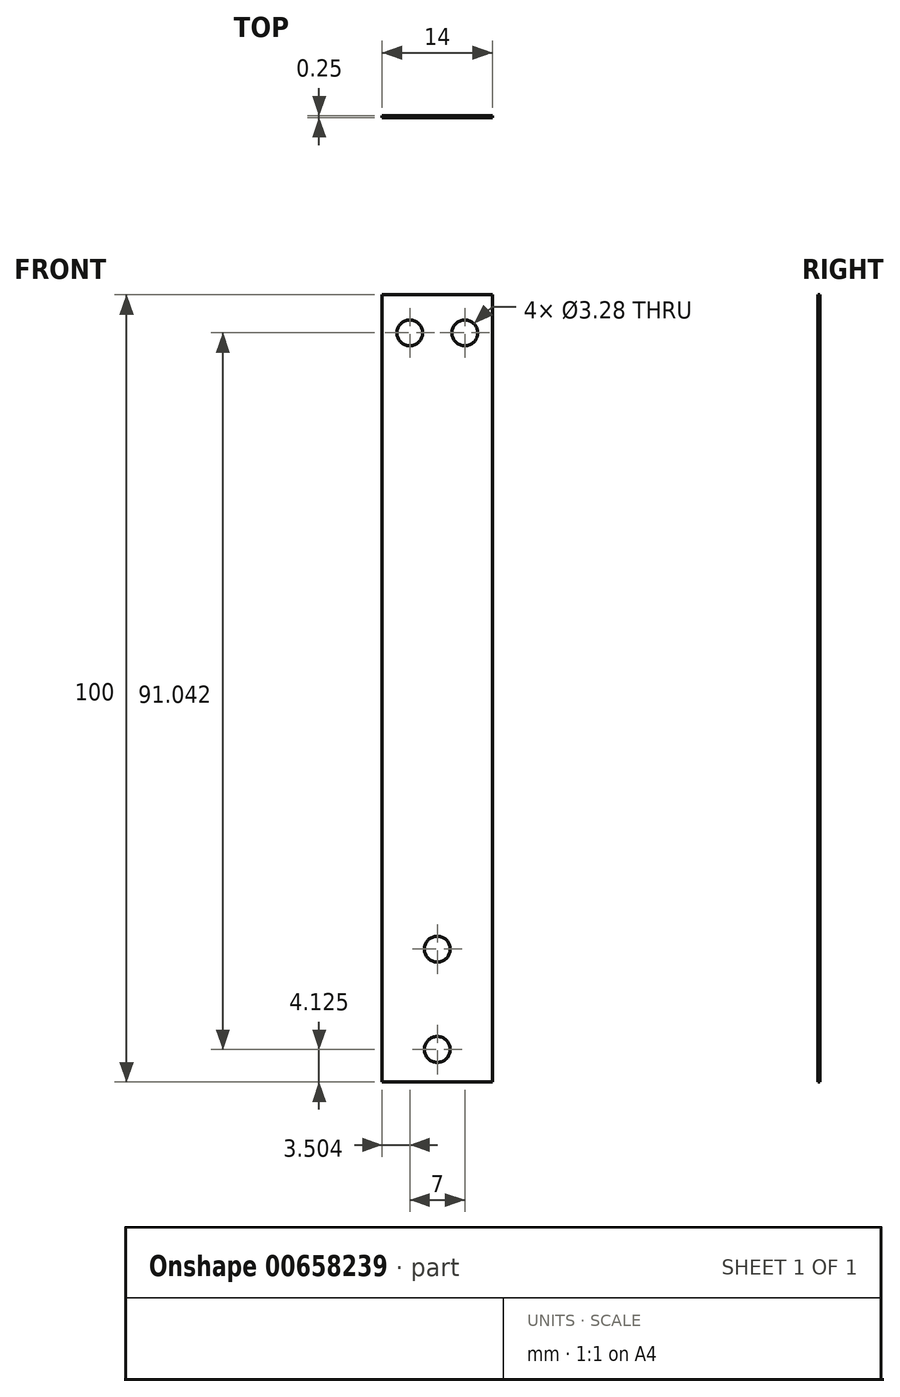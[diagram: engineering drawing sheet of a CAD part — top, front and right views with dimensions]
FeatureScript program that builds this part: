
annotation { "Feature Type Name" : "Feature", "Feature Type Description" : "" }
export const myFeature = defineFeature(function(context is Context, id is Id, definition is map)
    precondition{}
    {
        {
            var Q0;
            Q0=qCreatedBy(makeId("Front.planeOp"),FACE);
            var sketch = newSketch(context, id + "F0", { "sketchPlane" : qUnion([Q0])});
            skPoint(sketch, "E0.middle", {"position": v(-0.15, 1.7) * mm});
            skLineSegment(sketch, "E1.top", {"start": v(-7.15, -48.3) * mm, "end": v(6.85, -48.3) * mm});
            skLineSegment(sketch, "E1.right", {"start": v(6.85, 51.7) * mm, "end": v(6.85, -48.3) * mm});
            skLineSegment(sketch, "E2", {"start": v(5.85, 22.07) * mm, "end": v(5.85, 22.07) * mm});
            skLineSegment(sketch, "E3", {"start": v(-7.15, 51.7) * mm, "end": v(6.85, 51.7) * mm});
            skLineSegment(sketch, "E4", {"start": v(-7.15, -48.3) * mm, "end": v(-7.15, 51.7) * mm});
            skCircle(sketch, "E5", {"center": v(3.35, 46.86) * mm, "radius": 1.64 * mm});
            skCircle(sketch, "E6.MirrorC", {"center": v(-3.65, 46.86) * mm, "radius": 1.64 * mm});
            skCircle(sketch, "E7", {"center": v(-0.15, -31.43) * mm, "radius": 1.64 * mm});
            skCircle(sketch, "E8.MirrorC", {"center": v(-0.15, -44.18) * mm, "radius": 1.64 * mm});
            skSolve(sketch);
        }
        {
            var Q0;
            Q0 = qSketchRegion(id + "F0", true);
            extrude(context, id + "F1", {"entities" : qUnion([Q0]), "depth" : 0.25 * mm, "offsetDistance" : 25 * mm});
        }
    });
